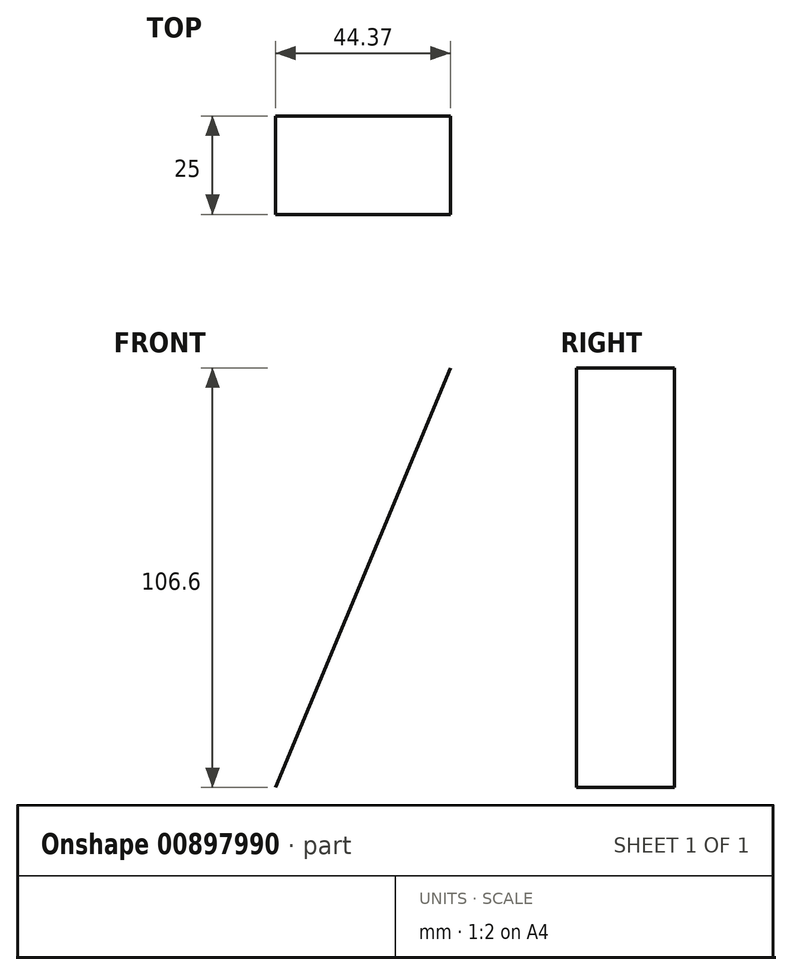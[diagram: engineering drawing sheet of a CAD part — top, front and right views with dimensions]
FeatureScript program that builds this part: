
annotation { "Feature Type Name" : "Feature", "Feature Type Description" : "" }
export const myFeature = defineFeature(function(context is Context, id is Id, definition is map)
    precondition{}
    {
        {
            var Q0;
            Q0=qCreatedBy(makeId("Front.planeOp"),FACE);
            var sketch = newSketch(context, id + "F0", { "sketchPlane" : qUnion([Q0])});
            skLineSegment(sketch, "E0", {"start": v(-130.6, -38.54) * mm, "end": v(-86.23, 68.06) * mm});
            skSolve(sketch);
        }
        {
            var Q0;
            Q0 = qSketchRegion(id + "F0", true);
            var Q1;
            Q1=sQuery(id+"F0.wireOp",EDGE,"E0");
            extrude(context, id + "F1", {"entities" : qUnion([Q0]), "bodyType" : ToolBodyType.SURFACE, "surfaceEntities" : qUnion([Q1]), "depth" : 25 * mm, "offsetDistance" : 25 * mm});
        }
    });
